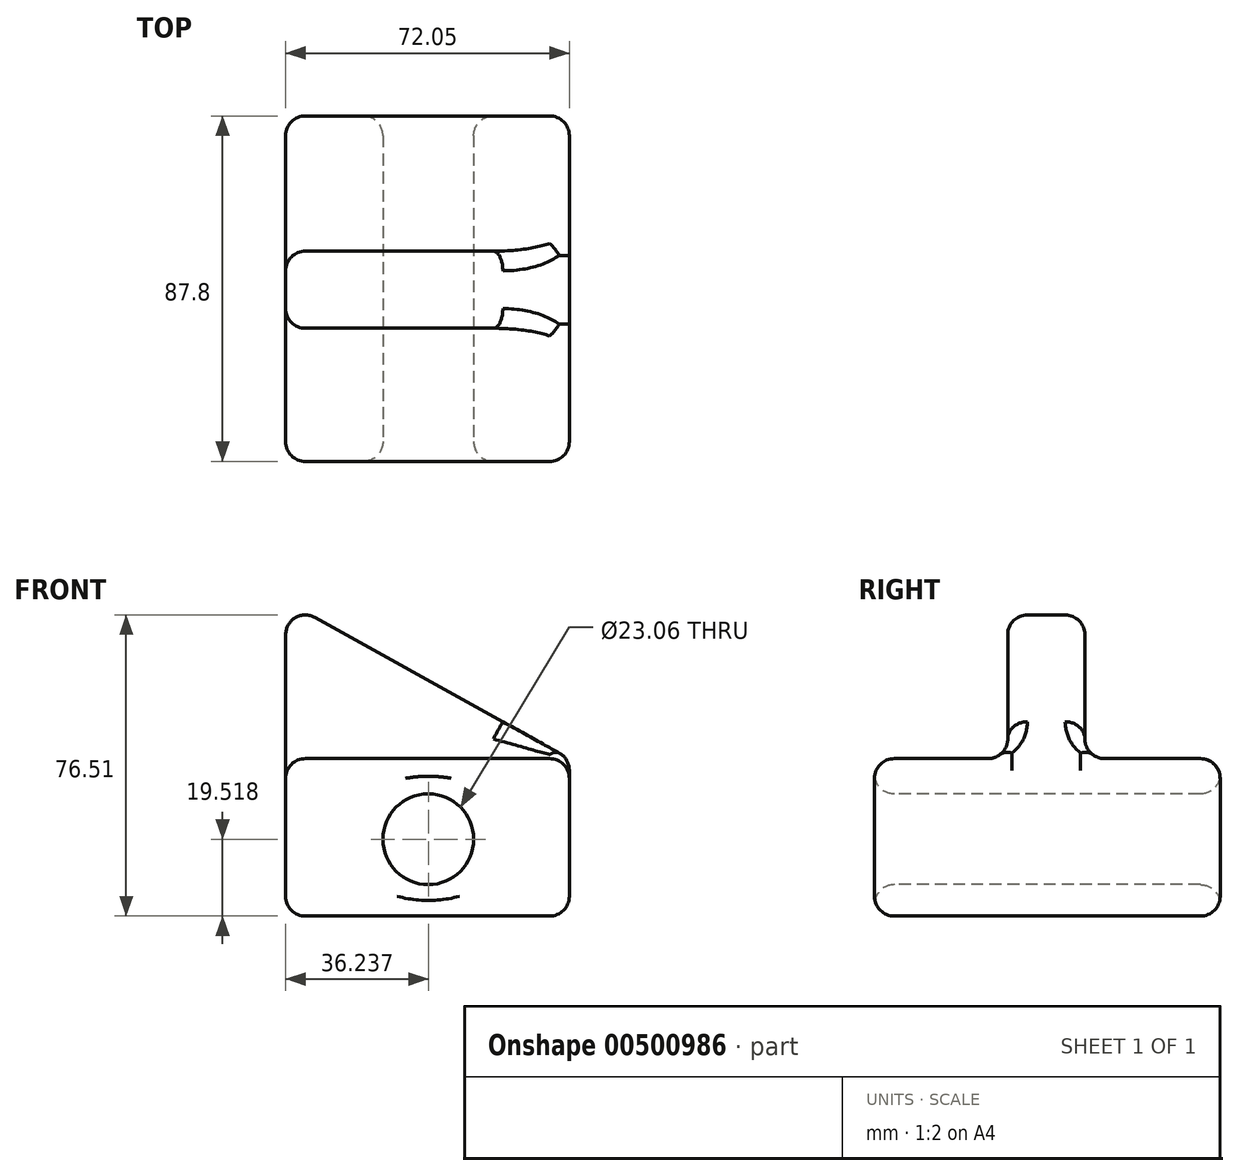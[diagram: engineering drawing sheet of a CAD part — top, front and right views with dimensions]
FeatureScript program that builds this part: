
annotation { "Feature Type Name" : "Feature", "Feature Type Description" : "" }
export const myFeature = defineFeature(function(context is Context, id is Id, definition is map)
    precondition{}
    {
        {
            var Q0;
            Q0=qCreatedBy(makeId("Top.planeOp"),FACE);
            var sketch = newSketch(context, id + "F0", { "sketchPlane" : qUnion([Q0])});
            skLineSegment(sketch, "E0.bottom", {"start": v(-59.89, -44.54) * mm, "end": v(12.16, -44.54) * mm});
            skLineSegment(sketch, "E0.top", {"start": v(-59.89, 43.26) * mm, "end": v(12.16, 43.26) * mm});
            skLineSegment(sketch, "E0.left", {"start": v(-59.89, -44.54) * mm, "end": v(-59.89, 43.26) * mm});
            skLineSegment(sketch, "E0.right", {"start": v(12.16, -44.54) * mm, "end": v(12.16, 43.26) * mm});
            skSolve(sketch);
        }
        {
            var Q0;
            Q0=makeQuery(id+"F0.imprint","IMPRINT",FACE,{"disambiguationData":[TD([[makeQuery(id+"F0.imprint","IMPRINT",EDGE,{"derivedFrom":sQuery(id+"F0.wireOp",EDGE,"E0.bottom")}),1.0]])]});
            extrude(context, id + "F1", {"entities" : qUnion([Q0]), "depth" : 40 * mm});
        }
        {
            var Q0;
            Q0=makeQuery(id+"F1.opExtrude","SWEPT_FACE",FACE,{"disambiguationData":[OSD([sQuery(id+"F0.wireOp",EDGE,"E0.bottom")])]});
            var sketch = newSketch(context, id + "F2", { "sketchPlane" : qUnion([Q0])});
            skCircle(sketch, "E1", {"center": v(-23.65, 19.52) * mm, "radius": 11.53 * mm});
            skSolve(sketch);
        }
        {
            var Q0;
            Q0=makeQuery(id+"F2.imprint","IMPRINT",FACE,{"disambiguationData":[TD([[makeQuery(id+"F2.imprint","IMPRINT",EDGE,{"derivedFrom":sQuery(id+"F2.wireOp",EDGE,"E1")}),1.0]])]});
            extrude(context, id + "F3", {"entities" : qUnion([Q0]), "operationType" : NewBodyOperationType.REMOVE, "endBound" : BoundingType.THROUGH_ALL, "oppositeDirection" : true, "depth" : 25 * mm});
        }
        {
            var Q0;
            Q0=makeQuery(id+"F1.opExtrude","CAP_FACE",FACE,{"disambiguationData":[OSD([sQuery(id+"F0.wireOp",EDGE,"E0.bottom"),sQuery(id+"F0.wireOp",EDGE,"E0.top"),sQuery(id+"F0.wireOp",EDGE,"E0.left"),sQuery(id+"F0.wireOp",EDGE,"E0.right")])],"isStart":false});
            var sketch = newSketch(context, id + "F4", { "sketchPlane" : qUnion([Q0])});
            skLineSegment(sketch, "E2.bottom", {"start": v(-59.89, -10.7) * mm, "end": v(12.16, -10.7) * mm});
            skLineSegment(sketch, "E2.top", {"start": v(-59.89, 8.88) * mm, "end": v(12.16, 8.88) * mm});
            skLineSegment(sketch, "E2.left", {"start": v(-59.89, -10.7) * mm, "end": v(-59.89, 8.88) * mm});
            skLineSegment(sketch, "E2.right", {"start": v(12.16, -10.7) * mm, "end": v(12.16, 8.88) * mm});
            skSolve(sketch);
        }
        {
            var Q0;
            Q0=makeQuery(id+"F4.imprint","IMPRINT",FACE,{"disambiguationData":[TD([[makeQuery(id+"F4.imprint","IMPRINT",EDGE,{"derivedFrom":sQuery(id+"F4.wireOp",EDGE,"E2.bottom")}),1.0]])]});
            extrude(context, id + "F5", {"entities" : qUnion([Q0]), "operationType" : NewBodyOperationType.ADD, "depth" : 40 * mm});
        }
        {
            var Q0;
            Q0=makeQuery(id+"F5.opExtrude","SWEPT_FACE",FACE,{"disambiguationData":[OSD([sQuery(id+"F4.wireOp",EDGE,"E2.bottom")])]});
            var sketch = newSketch(context, id + "F6", { "sketchPlane" : qUnion([Q0])});
            skLineSegment(sketch, "E3", {"start": v(12.16, 40) * mm, "end": v(-59.89, 80) * mm});
            skSolve(sketch);
        }
        {
            var Q0;
            Q0=makeQuery(id+"F6.imprint","IMPRINT",FACE,{"disambiguationData":[TD([[makeQuery(id+"F6.imprint","IMPRINT",EDGE,{"derivedFrom":sQuery(id+"F6.wireOp",EDGE,"E3")}),-1.0]])]});
            extrude(context, id + "F7", {"entities" : qUnion([Q0]), "operationType" : NewBodyOperationType.REMOVE, "endBound" : BoundingType.THROUGH_ALL, "oppositeDirection" : true, "depth" : 25 * mm});
        }
        {
            var Q0;
            Q0=makeQuery(id+"F5.opExtrude","SWEPT_FACE",FACE,{"disambiguationData":[OSD([sQuery(id+"F4.wireOp",EDGE,"E2.bottom")])]});
            var Q1;
            {var subQ0=sQuery(id+"F0.wireOp",EDGE,"E0.left");var subQ1=sQuery(id+"F0.wireOp",EDGE,"E0.right");var subQ2=sQuery(id+"F0.wireOp",EDGE,"E0.bottom");Q1=makeQuery(id+"F5.boolean.opBoolean","SPLIT",FACE,{"disambiguationData":[TD([makeQuery(id+"F1.opExtrude","SWEPT_FACE",FACE,{"disambiguationData":[OSD([subQ2])]})])],"derivedFrom":makeQuery(id+"F1.opExtrude","CAP_FACE",FACE,{"disambiguationData":[OSD([subQ2,sQuery(id+"F0.wireOp",EDGE,"E0.top"),subQ0,subQ1])],"isStart":false})});}
            var Q2;
            Q2=makeQuery(id+"F5.boolean.opBoolean","MERGE",FACE,{"derivedFrom":[makeQuery(id+"F1.opExtrude","SWEPT_FACE",FACE,{"disambiguationData":[OSD([sQuery(id+"F0.wireOp",EDGE,"E0.right")])]}),makeQuery(id+"F5.opExtrude","SWEPT_FACE",FACE,{"disambiguationData":[OSD([sQuery(id+"F4.wireOp",EDGE,"E2.right")])]})]});
            var Q3;
            {var subQ0=sQuery(id+"F0.wireOp",EDGE,"E0.right");var subQ1=sQuery(id+"F0.wireOp",EDGE,"E0.left");var subQ2=sQuery(id+"F0.wireOp",EDGE,"E0.top");Q3=makeQuery(id+"F5.boolean.opBoolean","SPLIT",FACE,{"disambiguationData":[TD([makeQuery(id+"F1.opExtrude","SWEPT_FACE",FACE,{"disambiguationData":[OSD([subQ2])]})])],"derivedFrom":makeQuery(id+"F1.opExtrude","CAP_FACE",FACE,{"disambiguationData":[OSD([sQuery(id+"F0.wireOp",EDGE,"E0.bottom"),subQ2,subQ1,subQ0])],"isStart":false})});}
            var Q4;
            Q4=makeQuery(id+"F1.opExtrude","SWEPT_FACE",FACE,{"disambiguationData":[OSD([sQuery(id+"F0.wireOp",EDGE,"E0.bottom")])]});
            var Q5;
            Q5=makeQuery(id+"F7.boolean.opBoolean","COPY",FACE,{"derivedFrom":makeQuery(id+"F7.opExtrude","SWEPT_FACE",FACE,{"disambiguationData":[OSD([sQuery(id+"F6.wireOp",EDGE,"E3")])]})});
            var Q6;
            Q6=makeQuery(id+"F1.opExtrude","SWEPT_FACE",FACE,{"disambiguationData":[OSD([sQuery(id+"F0.wireOp",EDGE,"E0.top")])]});
            var Q7;
            Q7=makeQuery(id+"F5.boolean.opBoolean","MERGE",FACE,{"derivedFrom":[makeQuery(id+"F1.opExtrude","SWEPT_FACE",FACE,{"disambiguationData":[OSD([sQuery(id+"F0.wireOp",EDGE,"E0.left")])]}),makeQuery(id+"F5.opExtrude","SWEPT_FACE",FACE,{"disambiguationData":[OSD([sQuery(id+"F4.wireOp",EDGE,"E2.left")])]})]});
            var Q8;
            Q8=makeQuery(id+"F1.opExtrude","CAP_FACE",FACE,{"disambiguationData":[OSD([sQuery(id+"F0.wireOp",EDGE,"E0.bottom"),sQuery(id+"F0.wireOp",EDGE,"E0.top"),sQuery(id+"F0.wireOp",EDGE,"E0.left"),sQuery(id+"F0.wireOp",EDGE,"E0.right")])],"isStart":true});
            fillet(context, id + "F8", {"entities" : qUnion([Q0, Q1, Q2, Q3, Q4, Q5, Q6, Q7, Q8]), "radius" : 5 * mm, "tangentPropagation" : true, "allowEdgeOverflow" : false});
        }
    });
